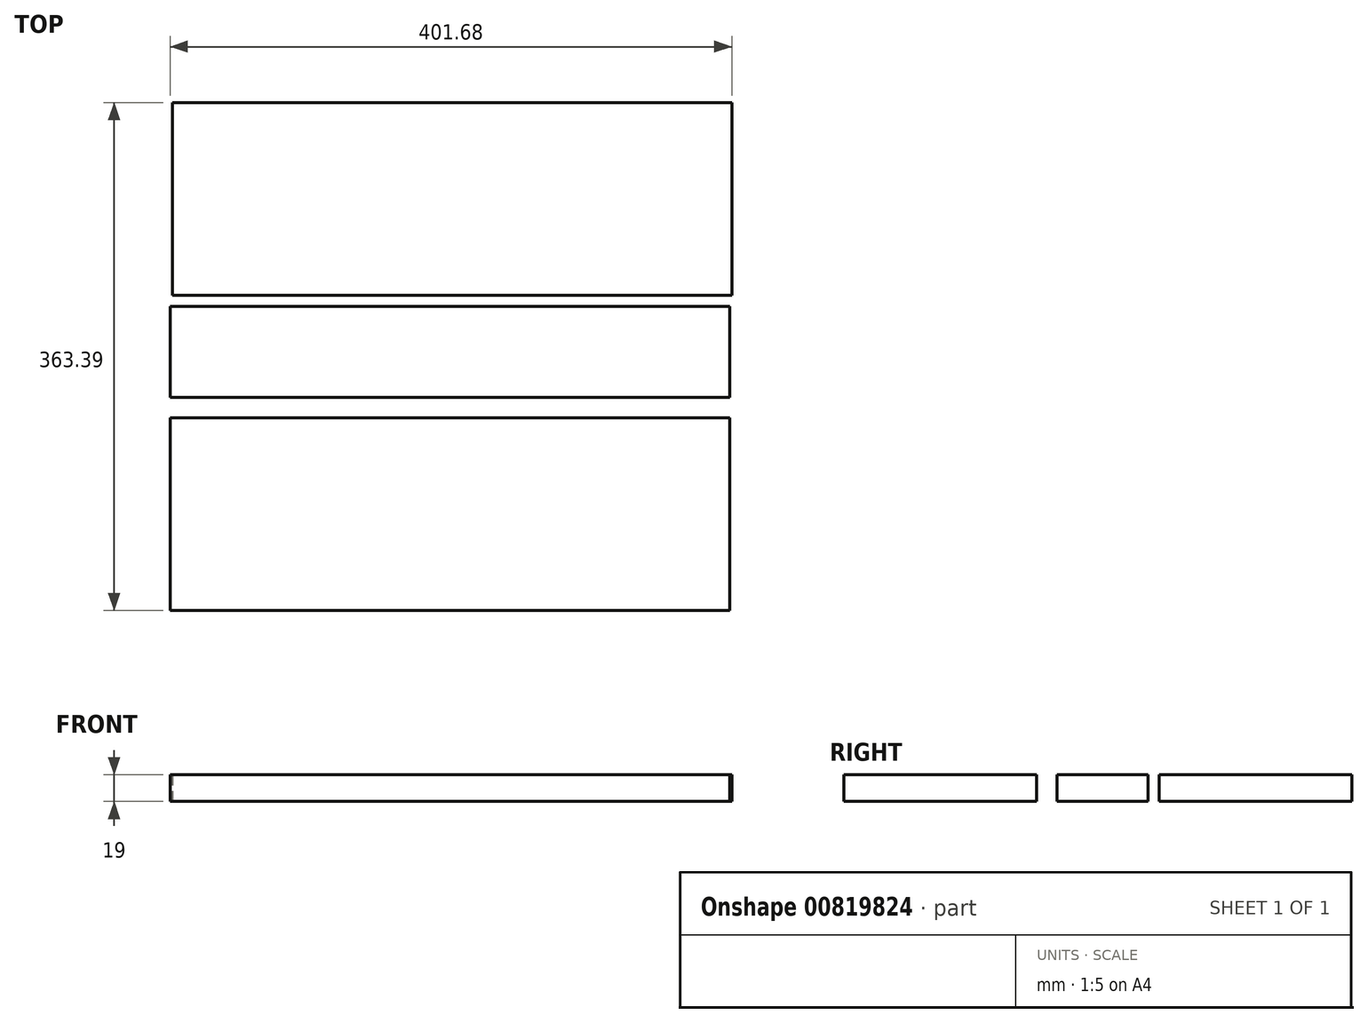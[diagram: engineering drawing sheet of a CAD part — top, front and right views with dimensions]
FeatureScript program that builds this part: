
annotation { "Feature Type Name" : "Feature", "Feature Type Description" : "" }
export const myFeature = defineFeature(function(context is Context, id is Id, definition is map)
    precondition{}
    {
        {
            var Q0;
            Q0=qCreatedBy(makeId("Top.planeOp"),FACE);
            var sketch = newSketch(context, id + "F0", { "sketchPlane" : qUnion([Q0])});
            skLineSegment(sketch, "E0.bottom", {"start": v(-327.88, 174.97) * mm, "end": v(72.12, 174.97) * mm});
            skLineSegment(sketch, "E0.top", {"start": v(-327.88, 36.97) * mm, "end": v(72.12, 36.97) * mm});
            skLineSegment(sketch, "E0.left", {"start": v(-327.88, 174.97) * mm, "end": v(-327.88, 36.97) * mm});
            skLineSegment(sketch, "E0.right", {"start": v(72.12, 174.97) * mm, "end": v(72.12, 36.97) * mm});
            skLineSegment(sketch, "E1.bottom", {"start": v(-329.31, 29.19) * mm, "end": v(70.69, 29.19) * mm});
            skLineSegment(sketch, "E1.top", {"start": v(-329.31, -35.81) * mm, "end": v(70.69, -35.81) * mm});
            skLineSegment(sketch, "E1.left", {"start": v(-329.31, 29.19) * mm, "end": v(-329.31, -35.81) * mm});
            skLineSegment(sketch, "E1.right", {"start": v(70.69, 29.19) * mm, "end": v(70.69, -35.81) * mm});
            skLineSegment(sketch, "E2.bottom", {"start": v(-329.56, -50.42) * mm, "end": v(70.44, -50.42) * mm});
            skLineSegment(sketch, "E2.top", {"start": v(-329.56, -188.42) * mm, "end": v(70.44, -188.42) * mm});
            skLineSegment(sketch, "E2.left", {"start": v(-329.56, -50.42) * mm, "end": v(-329.56, -188.42) * mm});
            skLineSegment(sketch, "E2.right", {"start": v(70.44, -50.42) * mm, "end": v(70.44, -188.42) * mm});
            skSolve(sketch);
        }
        {
            var Q0;
            Q0=makeQuery(id+"F0.imprint","IMPRINT",FACE,{"disambiguationData":[TD([[makeQuery(id+"F0.imprint","IMPRINT",EDGE,{"derivedFrom":sQuery(id+"F0.wireOp",EDGE,"E0.bottom")}),-1.0]])]});
            var Q1;
            Q1=makeQuery(id+"F0.imprint","IMPRINT",FACE,{"disambiguationData":[TD([[makeQuery(id+"F0.imprint","IMPRINT",EDGE,{"derivedFrom":sQuery(id+"F0.wireOp",EDGE,"E1.bottom")}),-1.0]])]});
            var Q2;
            Q2=makeQuery(id+"F0.imprint","IMPRINT",FACE,{"disambiguationData":[TD([[makeQuery(id+"F0.imprint","IMPRINT",EDGE,{"derivedFrom":sQuery(id+"F0.wireOp",EDGE,"E2.bottom")}),-1.0]])]});
            extrude(context, id + "F1", {"entities" : qUnion([Q0, Q1, Q2]), "depth" : 19 * mm, "offsetDistance" : 25 * mm});
        }
    });
